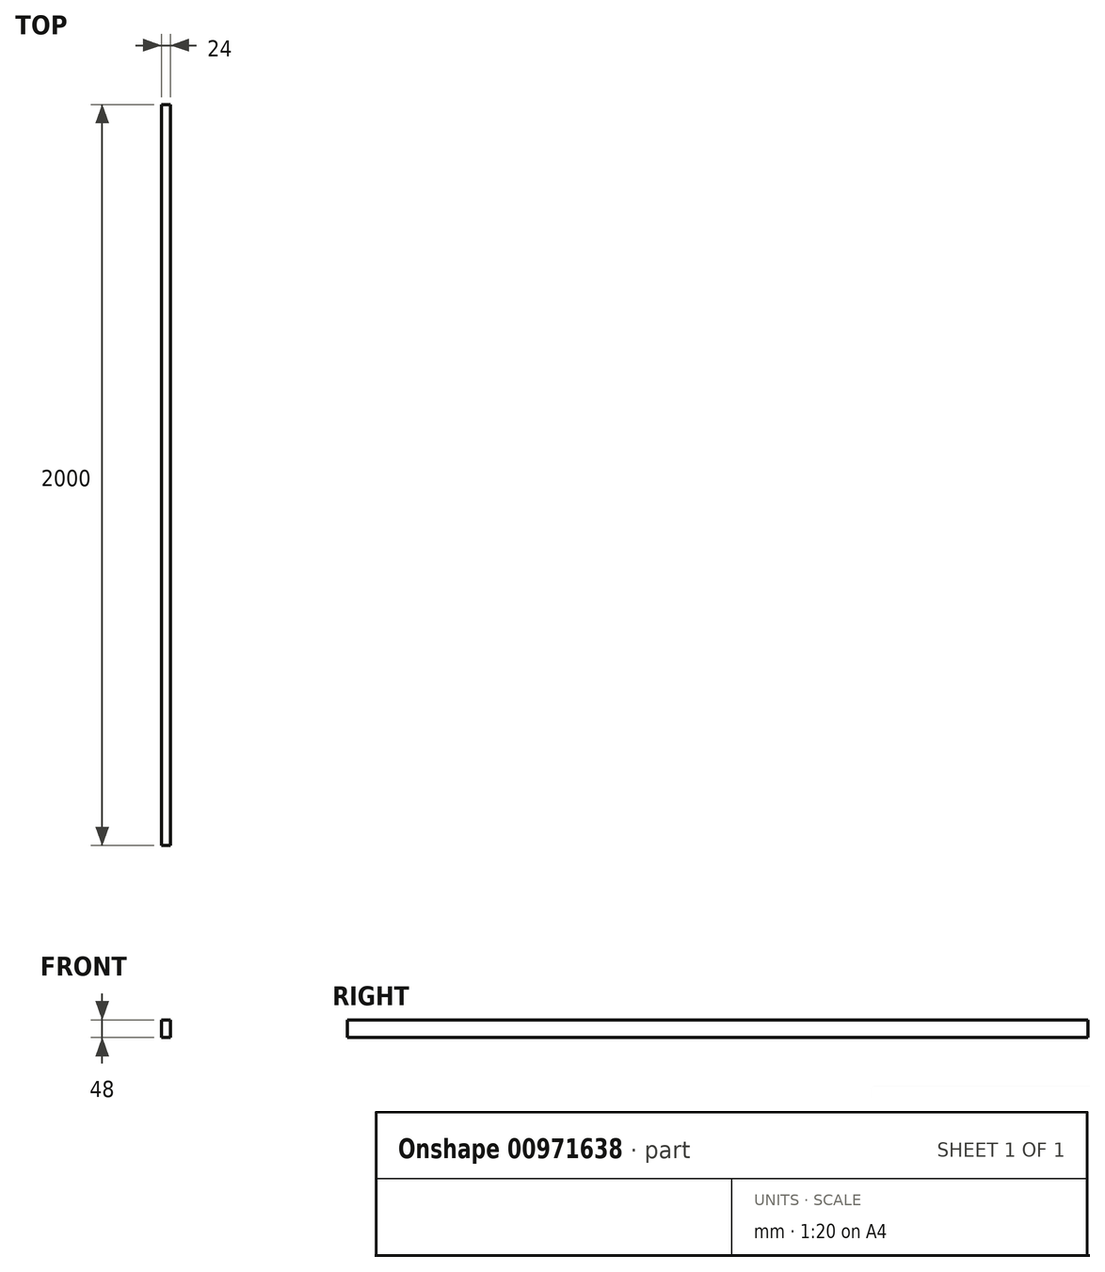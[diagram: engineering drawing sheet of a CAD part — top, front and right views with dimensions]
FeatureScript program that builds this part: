
annotation { "Feature Type Name" : "Feature", "Feature Type Description" : "" }
export const myFeature = defineFeature(function(context is Context, id is Id, definition is map)
    precondition{}
    {
        {
            assignVariable(context, id + "F0", {"name" : "c", "anyValue" : 2000});
        }
        {
            var Q0;
            Q0=qCreatedBy(makeId("Front.planeOp"),FACE);
            var sketch = newSketch(context, id + "F1", { "sketchPlane" : qUnion([Q0])});
            skLineSegment(sketch, "E0.bottom", {"start": v(12, -24) * mm, "end": v(-12, -24) * mm});
            skLineSegment(sketch, "E0.top", {"start": v(12, 24) * mm, "end": v(-12, 24) * mm});
            skLineSegment(sketch, "E0.left", {"start": v(12, -24) * mm, "end": v(12, 24) * mm});
            skLineSegment(sketch, "E0.right", {"start": v(-12, -24) * mm, "end": v(-12, 24) * mm});
            skPoint(sketch, "E0.middle", {"position": v(0, 0) * mm});
            skSolve(sketch);
        }
        {
            var Q0;
            Q0 = qSketchRegion(id + "F1", true);
            var Q1;
            Q1=makeQuery(id+"F1.imprint","IMPRINT",FACE,{"disambiguationData":[TD([[makeQuery(id+"F1.imprint","IMPRINT",EDGE,{"derivedFrom":sQuery(id+"F1.wireOp",EDGE,"E0.bottom")}),-1.0]])]});
            extrude(context, id + "F2", {"entities" : qUnion([Q0, Q1]), "depth" : (getVariable(context, 'c')) * mm, "offsetDistance" : 25 * mm});
        }
    });
